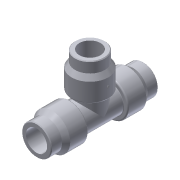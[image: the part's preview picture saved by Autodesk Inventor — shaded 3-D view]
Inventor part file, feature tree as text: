
AUTODESK INVENTOR PART (.ipt)
format: ipt  version: 2016 (Build 200138000, 138)  size: 307,712 bytes
history: native  units: in
note: dims shown in document units (in); Inventor stores cm internally (conversion verified against a paired STEP export)
features: sketch x16, extrude x15, chamfer x6, fillet x6, plane x3
ambient origin geometry x8: Origin, YZ Plane, XZ Plane, XY Plane, X Axis, Y Axis, Z Axis, Center Point
bodies: Solid1 (feature_tree)
feature tree (46):
  extrude  "mainBody"  Depth=4.3701in TaperAngle=0.0deg
  sketch  "Sketch10"  dims[d0=1.1417in d1=4.3701in d2=0.0in]
  plane  "Work Plane5"
  extrude  "TBody"  Depth=2.185in
  extrude  "TSocket"  Depth=0.8661in
  extrude  "TTube"  Depth=0.7874in
  extrude  "mainTube"  Depth=0.7874in
  extrude  "mainSocket1"  Depth=0.8661in
  extrude  "mainSocket2"  Depth=0.8661in
  sketch  "Sketch21"  dims[d53=1.5551in d54=0.0in d73=0.9055in]
  plane  "Work Plane6"
  extrude  "Extrusion18"  Depth=0.9055in
  extrude  "Extrusion19"  Depth=1.4961in
  extrude  "Extrusion20"  Depth=1.2205in
  chamfer  "Chamfer1"  Distance=0.4331in
  fillet  "Fillet1"  Radius=0.0591in
  fillet  "Fillet2"  Radius=0.0197in
  chamfer  "Chamfer2"  Distance=0.0295in Angle=30.0deg
  extrude  "Extrusion21"  Depth=1.378in TaperAngle=0.0deg
  extrude  "Extrusion22"  Depth=0.4331in TaperAngle=0.0deg
  chamfer  "Chamfer3"  Distance=0.1969in Angle=30.0deg
  fillet  "Fillet5"  Radius=0.0197in
  fillet  "Fillet4"  Radius=0.0591in
  chamfer  "Chamfer4"  Distance=0.0295in Angle=30.0deg
  extrude  "Extrusion23"  Depth=1.378in TaperAngle=0.0deg
  extrude  "Extrusion24"  Depth=0.4331in TaperAngle=0.0deg
  chamfer  "Chamfer5"  Distance=0.1969in Angle=30.0deg
  fillet  "Fillet6"  Radius=0.0591in
  fillet  "Fillet7"  Radius=0.0197in
  chamfer  "Chamfer6"  Distance=0.0295in Angle=30.0deg
  plane  "Work Plane7"
  extrude  "Extrusion25"  Depth=0.1in
  sketch  "Sketch11"  dims[d29=2.185in d30=1.1417in]
  sketch  "Sketch12"  dims[d31=1.5748in d32=0.5512in d33=0.0in d34=0.0in d35=0.8661in]
  sketch  "Sketch13"  dims[d37=1.5551in d38=0.0in d39=0.7874in]
  sketch  "Sketch14"  dims[d41=0.6in d42=0.0in d43=0.7874in]
  sketch  "Sketch15"  dims[d45=7.0in d46=0.0in d47=0.8661in]
  sketch  "Sketch16"  dims[d49=1.5551in d50=0.0in d51=0.8661in]
  sketch  "Sketch22"  dims[d74=0.01in d75=0.0in d76=1.4961in]
  sketch  "Sketch23"  dims[d77=1.4173in d78=0.0in d79=1.2205in d80=0.4331in d81=0.0in]
  sketch  "Sketch24"  dims[d82=0.1969in d83=0.1378in d84=45.0deg d85=0.0591in d86=0.0197in d87=0.0295in d88=0.1378in d89=30.0deg]
  sketch  "Sketch25"  dims[d90=1.4961in d91=1.378in d92=0.0in]
  sketch  "Sketch26"  dims[d93=1.2205in d94=0.4331in d95=0.0in d96=0.1969in d97=0.1378in d98=30.0deg d100=0.0197in d101=0.0591in d102=0.0295in d103=0.1378in d104=30.0deg]
  sketch  "Sketch27"  dims[d105=1.4961in d106=1.378in d107=0.0in]
  sketch  "Sketch28"  dims[d108=1.2205in d109=0.4331in d110=0.0in d111=0.1969in d112=0.1378in d113=30.0deg d114=0.0591in d115=0.0197in d116=0.0295in d117=0.1378in d118=30.0deg]
  sketch  "Sketch29"  dims[d119=0.752in d120=0.1in d121=1.1811in d122=0.0787in d123=0.0in]
